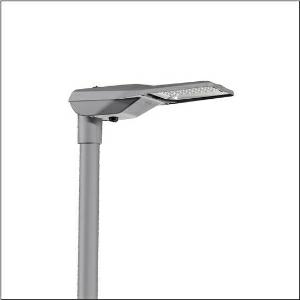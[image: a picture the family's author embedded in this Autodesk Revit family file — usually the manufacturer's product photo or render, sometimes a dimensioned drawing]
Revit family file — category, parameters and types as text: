
# Revit family: streetlight_sl_21_iq_mini___st0_8a_5xe2c31y08hb_5d56
name_source: partatom
category: Lighting Fixtures
units: mm (PartAtom-declared; Revit-internal decimal feet)

## family parameters
Cut with Voids When Loaded = No
Host = Face
Light Source = No
Part Type = Normal
Room Calculation Point = No
Round Connector Dimension = Use Diameter
Shared = No

## types (1)
- --- (1 x LED, 9750 lm, 71 W, 3000K)
    Apparent Load = 71 VA
    CIE Flux Codes = 38 75 97 100 100
    Color Rendering = 70
    Color Temperature = 3000K
    Default Elevation = 1800 mm
    Description = Streetlight SL 21 iQ mini, mast luminaire, primary light control with lens, of PMMA, primary optical cover: cover, of toughened safety glass, transparent, light distribution: ST0.8a, light emission: direct distribution, primary light characteristic: asymmetric, installation type: post-top, side-entry, LED, High Power LED, rated luminous flux: 9.750lm, luminous efficacy: 137lm/W, light colour: 730, colour temperature: 3000K, control gear: iQ-Street Remote, D4i with power reduction, control: pre-setting: logarithmic dimming characteristic, Street-Remote, Auto-Match, Temp-Guard, Lumen-Switch, Night-Set, Smart-Wire, Light-Fading, Desk-Remote (wireless, voltage-free reading and setting of iQ features in the workshop via application-optimized NFC function/RFID function), optimised constant luminous flux control (CLO 2.0), mains connection: 220..240V, AC, 50/60Hz, start of lifetime: 71W, end of service life: 75W, reduction: 30W, luminaire housing, of diecast aluminium, powder-coated, Siteco® metallic grey (DB 702S), corrosivity category C5 mid according to DIN EN ISO 12944, please order mast flange separately, inclination adjustable: 0°, 5°, 10°, 15°, sealing non-destructively replaceable, multi-level sealing system, length: 628mm, width: 235mm, height: 110mm, mast flange for spigot size: 42mm (side-entry): 5XC10008XM4, 60/48mm (side-entry/post-top): 5XC10108XM2, 76/60mm (side-entry/post-top): 5XC10108XM1, mounting height: 4..8m, Smart Interface below and above, protection rating (complete): IP66, insulation class (complete): insulation class II (safety insulation), certification: CE, ENEC, ENEC+, VDE, impact resistance: IK10, permissible operating ambient temperature for outdoor applications: -40..+50°C, standard-compliant lighting for roads and squares, packaging unit: 1 piece

Light Distribution: ST0.8a
    Height = 110 mm
    Lamp = 1 x LED
    Lamp Light Flux = 9750 lm
    Lamp Power = 71 W
    Lamp count = 1
    Length = 625 mm
    Luminous efficacy = 137 lm/W
    Manufacturer = Siteco
    ModVariant = No
    Model = 5XE2C31Y08HB
    Number of Poles = 1
    OnlyDefault = Yes
    Power Factor = 1
    Product Name = Streetlight SL 21 iQ mini | ST0.8a
    Product group = mast luminaire | pylon top
    ProductGroupID = 6100
    Protection Class = Protection class II
    Protection Degree = IP 66
    RLX_Detail_Level = 1
    RLX_Emergency_Light_Flux = 0 lm
    RLX_Emergency_Type = 0
    RLX_Emergency_Type_DB = No
    RlxData = <blob elided: 26713 chars, md5=8c9de64d>
    Socket = socket
    Standby Power = 0 W
    System Light Flux = 9750 lm
    System Power = 71 W
    Type Comments = factory setting: luminous flux: 100 % | dim-lin: 254 | 716 mA
    Type Image = l_1003514.jpg
    URL = http://relux.com
    VarID = @adj_113308
    Voltage = 0 V
    Weight = 0.00 kg
    Width = 234 mm

## geometry (parser evidence)
native form markers: Blend x4, Sweep x10
no freeform markers — native parametric forms only
